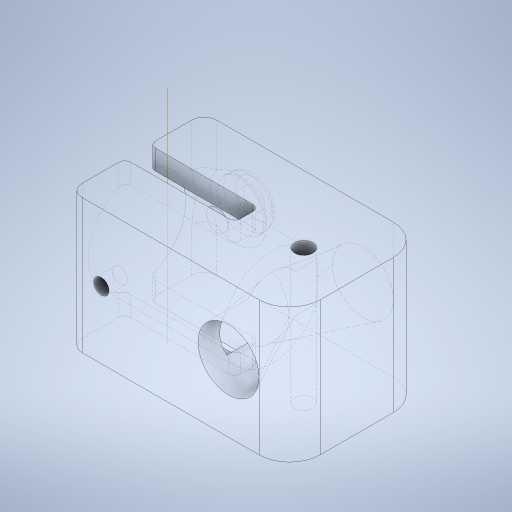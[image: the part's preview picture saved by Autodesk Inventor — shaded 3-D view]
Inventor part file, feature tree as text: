
AUTODESK INVENTOR PART (.ipt)
format: ipt  version: 2023 (Build 270158000, 158)  size: 491,520 bytes
history: native  units: in
note: dims shown in document units (in); Inventor stores cm internally (conversion verified against a paired STEP export)
features: sketch x8, extrude x7, fillet x4, loft x2, other x1
ambient origin geometry x8: Origin, YZ Plane, XZ Plane, XY Plane, X Axis, Y Axis, Z Axis, Center Point
bodies: Solid1 (feature_tree)
feature tree (22):
  extrude  "Extrusion1"  Depth=0.8661in
  sketch  "Sketch3"  dims[d2=0.8661in d3=0.0in d4=0.1772in]
  extrude  "Extrusion2"  Depth=0.8661in
  extrude  "Extrusion3"  Depth=0.8787in
  extrude  "Extrusion4"  Depth=0.8661in
  other  "Work Axis1"
  extrude  "Extrusion5"  Depth=0.8661in TaperAngle=0.0deg
  sketch  "Sketch10"  dims[d11=0.8697in d12=0.0in d13=0.8661in d14=0.0in]
  extrude  "Extrusion6"  Depth=0.2039in
  extrude  "Extrusion7"  Depth=0.3937in TaperAngle=0.0deg
  fillet  "Fillet1"  Radius=0.1378in
  fillet  "Fillet2"  Radius=0.315in
  fillet  "Fillet3"  Radius=0.3937in
  sketch  "Sketch11"  dims[d30=0.0984in d31=0.2039in]
  loft  "Loft4"
  loft  "Loft5"
  fillet  "Fillet7"  Radius=0.1575in
  sketch  "Sketch2"  dims[d0=1.4173in d1=0.8661in]
  sketch  "Sketch4"  dims[d5=0.1181in d6=0.8787in]
  sketch  "Sketch9"  dims[d7=0.8661in d8=0.0in d10=0.6299in]
  sketch  "Sketch12"  dims[d32=0.0984in d33=0.3937in d34=0.0in d35=0.1378in d36=0.315in d37=0.3937in d38=0.0in]
  sketch  "Sketch13"  dims[d39=0.1181in d40=0.0in d41=0.0394in d42=0.0787in d43=0.1575in d44=0.0394in d46=1.4173in d47=0.7087in d48=0.1969in d49=1.0236in d50=0.3937in d51=0.0in d52=90.0deg d53=0.0in d54=90.0deg d55=0.3937in d56=1.0236in d57=0.3937in d58=0.0in d59=90.0deg d60=0.0in d61=90.0deg d70=0.1969in]
